# Revit family: QF_HACKMAN_4215353
name_source: partatom
category: Specialty Equipment
revit_build: Autodesk Revit Architecture 2012 (Build: 20110916_2132(x64)
units: mm (PartAtom-declared; Revit-internal decimal feet)

## types (1)
- QF_HACKMAN_4215353
    Apparent Power = 43596 VA
    Cold Water Connection Height = 380 mm
    Cold Water Maximum Pressure = 0.00 psi
    Cold Water Minimum Pressure = 0.00 psi
    Cold Water Size = 1"
    Cold Water Temperature Recommended = -460 °F
    Conn Conduit = Yes
    Cycle = 50 Hz
    Depth = 940 mm  [stored 3.08399 ft]
    Description = COMBI KETTLE VIKING COMBI 200E
    Elec Conn Connection Height = 635 mm
    FL Amps = 63 A
    Height = 1040 mm  [stored 3.41207 ft]
    Hot Water Connection Height = 700 mm  [stored 2.29659 ft]
    Hot Water Consumption = 0 GPM
    Hot Water Maximum Pressure = 0.00 psi
    Hot Water Minimum Pressure = 0.00 psi
    Hot Water Size = 1"
    Hot Water Temperature = -460 °F
    Indirect Waste Connection Height = 0 mm  [stored 0 ft]
    Indirect Waste Size = 0"
    Manufacturer = HACKMAN
    Max Overcurrent Protection = 0 A
    Min Ckt Ampacity = 0 A
    Model = 4215353
    Overall Height = 1535 mm
    Phase = 3
    Volts = 400 V
    Waste Water Discharge Temperature = -460 °F
    Watts = 31500 W
    Weight in Pounds = 278
    Width = 1360 mm  [stored 4.46194 ft]

note: [stored X ft] marks values corroborated as IEEE doubles in the binary element streams (Revit-internal decimal feet)

## geometry (parser evidence)
native form markers: Blend x27, Sweep x2
no freeform markers — native parametric forms only
